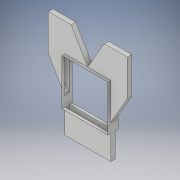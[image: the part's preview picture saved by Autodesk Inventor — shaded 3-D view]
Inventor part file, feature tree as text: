
AUTODESK INVENTOR PART (.ipt)
format: ipt  version: 2017 (Build 210142000, 142)  size: 152,064 bytes
history: native  units: in
note: dims shown in document units (in); Inventor stores cm internally (conversion verified against a paired STEP export)
features: other x4, delete_face x1, sketch x1
ambient origin geometry x8: Origin, YZ Plane, XZ Plane, XY Plane, X Axis, Y Axis, Z Axis, Center Point
bodies: Solid1 (feature_tree)
feature tree (6):
  other  "end door frame (100).ipt"
  delete_face  "Delete Face1"
  sketch  "Sketch2"  dims[d0=0.0354in]
  other  "connection for doors"
  other  "rame of door::end door frame (100).ipt"
  other  "TaggingFeature1"
